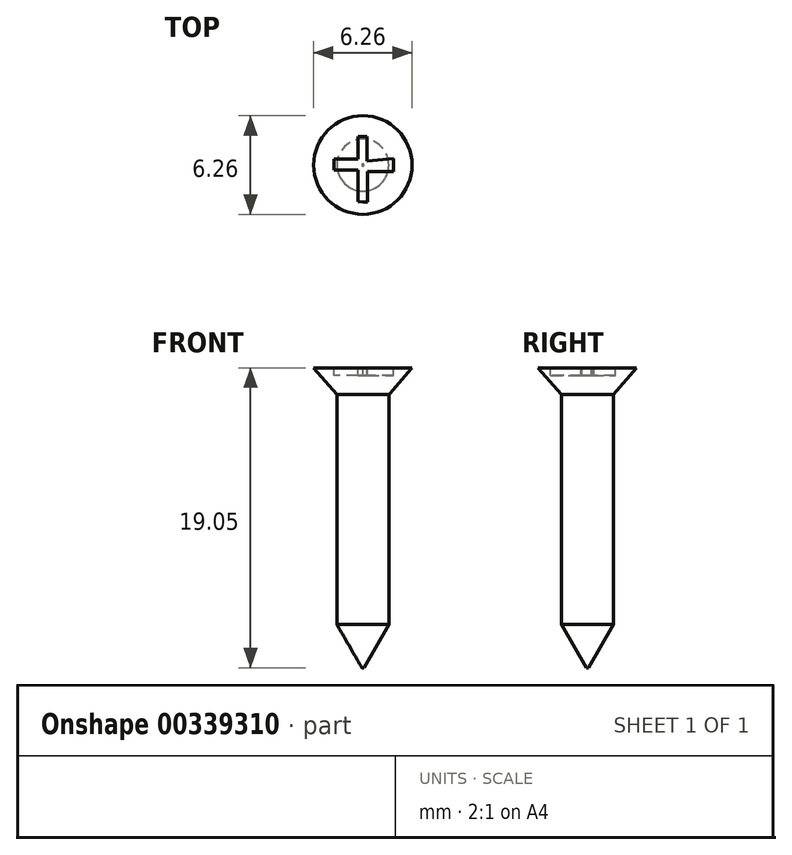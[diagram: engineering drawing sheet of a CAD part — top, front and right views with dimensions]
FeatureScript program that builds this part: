
annotation { "Feature Type Name" : "Feature", "Feature Type Description" : "" }
export const myFeature = defineFeature(function(context is Context, id is Id, definition is map)
    precondition{}
    {
        {
            var Q0;
            Q0=qCreatedBy(makeId("Top.planeOp"),FACE);
            var sketch = newSketch(context, id + "F0", { "sketchPlane" : qUnion([Q0])});
            skCircle(sketch, "E0", {"center": v(0, 0) * mm, "radius": 1.65 * mm});
            skSolve(sketch);
        }
        {
            var Q0;
            Q0=makeQuery(id+"F0.imprint","IMPRINT",FACE,{"disambiguationData":[TD([[makeQuery(id+"F0.imprint","IMPRINT",EDGE,{"derivedFrom":sQuery(id+"F0.wireOp",EDGE,"E0")}),1.0]])]});
            extrude(context, id + "F1", {"entities" : qUnion([Q0]), "depth" : 1.7 * mm, "hasDraft" : true, "draftAngle" : 41 * degree});
        }
        {
            var Q0;
            Q0=qCreatedBy(makeId("Front.planeOp"),FACE);
            var sketch = newSketch(context, id + "F2", { "sketchPlane" : qUnion([Q0])});
            skPoint(sketch, "E1", {"position": v(0, -17.35) * mm});
            skSolve(sketch);
        }
        {
            var Q0;
            Q0=makeQuery(id+"F1.opExtrude","CAP_FACE",FACE,{"disambiguationData":[OSD([sQuery(id+"F0.wireOp",EDGE,"E0")])],"isStart":true});
            var Q1;
            Q1=sQuery(id+"F2.wireOp",VERTEX,"E1");
            extrude(context, id + "F3", {"entities" : qUnion([Q0]), "operationType" : NewBodyOperationType.ADD, "endBound" : BoundingType.UP_TO_VERTEX, "endBoundEntityVertex" : qUnion([Q1]), "depth" : 25 * mm});
        }
        {
            var Q0;
            Q0=makeQuery(id+"F3.opExtrude","CAP_EDGE",EDGE,{"disambiguationData":[OSD([sQuery(id+"F0.wireOp",EDGE,"E0")])],"isStart":false});
            chamfer(context, id + "F4", {"entities" : qUnion([Q0]), "chamferType" : ChamferType.OFFSET_ANGLE, "width" : 2.75 * mm, "oppositeDirection" : false, "angle" : 30 * degree, "tangentPropagation" : true});
        }
        {
            var Q0;
            Q0=makeQuery(id+"F1.opExtrude","CAP_FACE",FACE,{"disambiguationData":[OSD([sQuery(id+"F0.wireOp",EDGE,"E0")])],"isStart":false});
            var sketch = newSketch(context, id + "F5", { "sketchPlane" : qUnion([Q0])});
            skLineSegment(sketch, "E2", {"start": v(0, -2.34) * mm, "end": v(0.28, -2.34) * mm});
            skLineSegment(sketch, "E3", {"start": v(0.28, -2.34) * mm, "end": v(0.28, -0.41) * mm});
            skLineSegment(sketch, "E4", {"start": v(0.28, -0.41) * mm, "end": v(1.95, -0.41) * mm});
            skLineSegment(sketch, "E5", {"start": v(1.95, -0.41) * mm, "end": v(1.95, 0.4) * mm});
            skLineSegment(sketch, "E6", {"start": v(1.95, 0.4) * mm, "end": v(0.27, 0.26) * mm});
            skLineSegment(sketch, "E7", {"start": v(0.27, 0.26) * mm, "end": v(0.27, 1.8) * mm});
            skLineSegment(sketch, "E8", {"start": v(0.27, 1.8) * mm, "end": v(-0.3, 1.8) * mm});
            skLineSegment(sketch, "E9", {"start": v(-0.3, 1.8) * mm, "end": v(-0.3, 0.4) * mm});
            skLineSegment(sketch, "E10", {"start": v(-0.3, 0.4) * mm, "end": v(-1.84, 0.4) * mm});
            skLineSegment(sketch, "E11", {"start": v(-1.84, 0.4) * mm, "end": v(-1.84, -0.33) * mm});
            skLineSegment(sketch, "E12", {"start": v(-1.84, -0.33) * mm, "end": v(-0.3, -0.33) * mm});
            skLineSegment(sketch, "E13", {"start": v(-0.3, -0.33) * mm, "end": v(-0.3, -2.33) * mm});
            skLineSegment(sketch, "E14", {"start": v(-0.3, -2.33) * mm, "end": v(0, -2.34) * mm});
            skSolve(sketch);
        }
        {
            var Q0;
            Q0=makeQuery(id+"F5.imprint","IMPRINT",FACE,{"disambiguationData":[TD([[makeQuery(id+"F5.imprint","IMPRINT",EDGE,{"derivedFrom":sQuery(id+"F5.wireOp",EDGE,"E2")}),1.0]])]});
            extrude(context, id + "F6", {"entities" : qUnion([Q0]), "operationType" : NewBodyOperationType.REMOVE, "oppositeDirection" : true, "depth" : 0.5 * mm});
        }
    });
